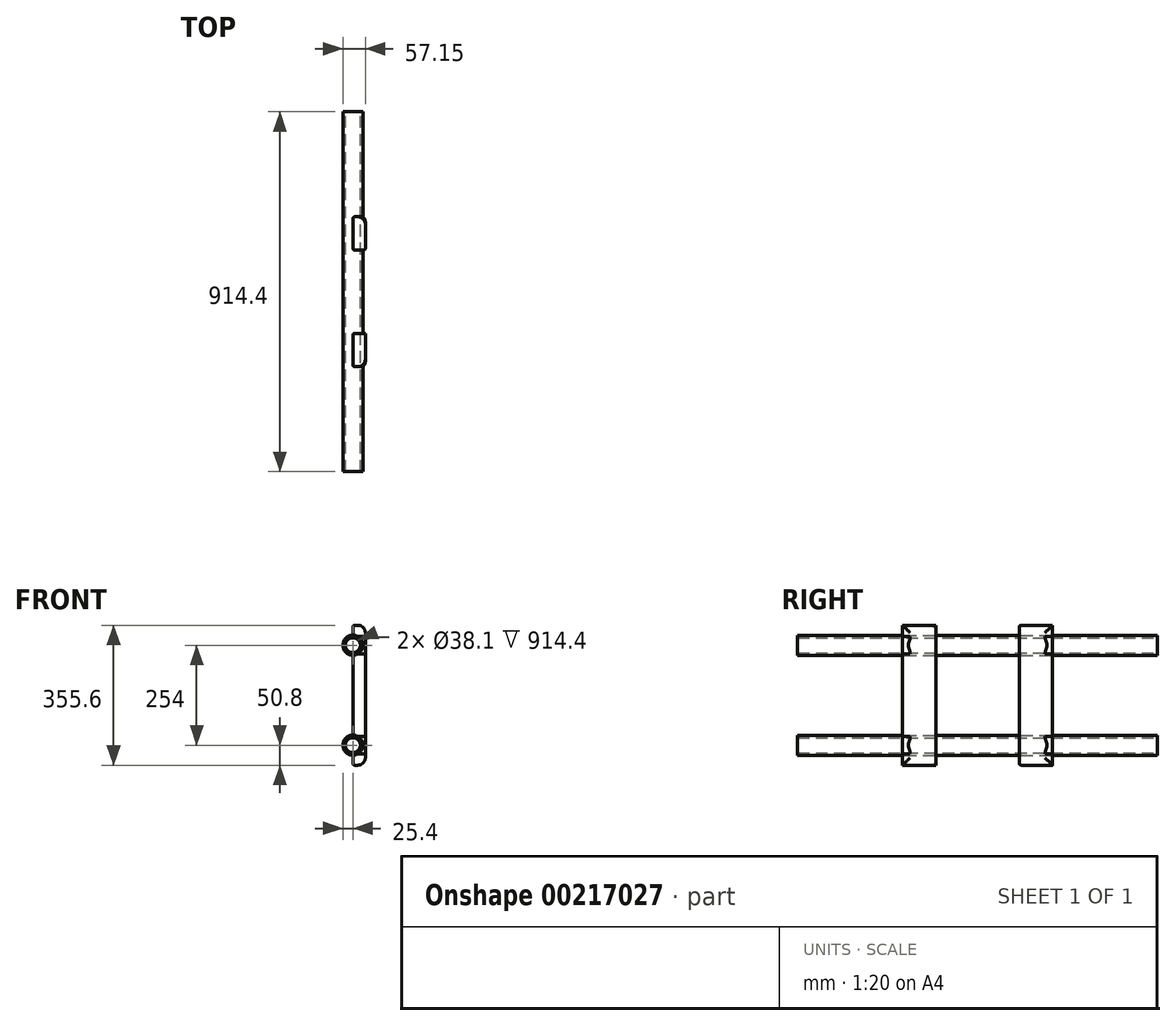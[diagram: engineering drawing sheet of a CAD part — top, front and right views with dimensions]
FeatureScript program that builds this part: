
annotation { "Feature Type Name" : "Feature", "Feature Type Description" : "" }
export const myFeature = defineFeature(function(context is Context, id is Id, definition is map)
    precondition{}
    {
        {
            var Q0;
            Q0=qCreatedBy(makeId("Front.planeOp"),FACE);
            var sketch = newSketch(context, id + "F0", { "sketchPlane" : qUnion([Q0])});
            skLineSegment(sketch, "E0", {"start": v(0, 0) * mm, "end": v(0, 76.2) * mm, "construction": true});
            skLineSegment(sketch, "E1", {"start": v(0, 76.2) * mm, "end": v(0, 0) * mm, "construction": true});
            skLineSegment(sketch, "E2", {"start": v(0, 0) * mm, "end": v(0, -76.2) * mm, "construction": true});
            skCircle(sketch, "E3", {"center": v(0, -76.2) * mm, "radius": 25.4 * mm});
            skCircle(sketch, "E4", {"center": v(0, -76.2) * mm, "radius": 19.05 * mm});
            skLineSegment(sketch, "E5", {"start": v(0, 101.6) * mm, "end": v(0, 127) * mm});
            skLineSegment(sketch, "E6", {"start": v(0, -101.6) * mm, "end": v(0, -127) * mm});
            skLineSegment(sketch, "E7", {"start": v(0, -127) * mm, "end": v(31.75, -127) * mm});
            skLineSegment(sketch, "E8", {"start": v(31.75, -127) * mm, "end": v(31.75, 127) * mm});
            skLineSegment(sketch, "E9", {"start": v(0, 50.8) * mm, "end": v(0, -50.8) * mm});
            skLineSegment(sketch, "E10", {"start": v(0, 0) * mm, "end": v(0, 177.8) * mm});
            skCircle(sketch, "E11", {"center": v(0, 177.8) * mm, "radius": 25.4 * mm});
            skCircle(sketch, "E12", {"center": v(0, 177.8) * mm, "radius": 19.05 * mm});
            skLineSegment(sketch, "E13", {"start": v(0, 203.2) * mm, "end": v(0, 228.6) * mm});
            skLineSegment(sketch, "E14", {"start": v(0, 228.6) * mm, "end": v(31.75, 228.6) * mm});
            skLineSegment(sketch, "E15", {"start": v(31.75, 228.6) * mm, "end": v(31.75, 127) * mm});
            skSolve(sketch);
        }
        {
            var Q0;
            {var subQ0=sQuery(id+"F0.wireOp",EDGE,"E6");Q0=makeQuery(id+"F0.imprint","IMPRINT",FACE,{"disambiguationData":[TD([[makeQuery(id+"F0.imprint","IMPRINT",EDGE,{"derivedFrom":subQ0}),1.0]])]});}
            extrude(context, id + "F1", {"entities" : qUnion([Q0]), "depth" : 381 * mm, "symmetric" : true});
        }
        {
            var Q0;
            Q0=makeQuery(id+"F1.opExtrude","SWEPT_FACE",FACE,{"disambiguationData":[OSD([sQuery(id+"F0.wireOp",EDGE,"E8"),sQuery(id+"F0.wireOp",EDGE,"E15")])]});
            var sketch = newSketch(context, id + "F2", { "sketchPlane" : qUnion([Q0])});
            skLineSegment(sketch, "E16.bottom", {"start": v(105.61, -155.17) * mm, "end": v(-105.61, -155.17) * mm});
            skLineSegment(sketch, "E16.top", {"start": v(105.61, 256.77) * mm, "end": v(-105.61, 256.77) * mm});
            skLineSegment(sketch, "E16.left", {"start": v(105.61, -155.17) * mm, "end": v(105.61, 256.77) * mm});
            skLineSegment(sketch, "E16.right", {"start": v(-105.61, -155.17) * mm, "end": v(-105.61, 256.77) * mm});
            skPoint(sketch, "E16.middle", {"position": v(0, 50.8) * mm});
            skPoint(sketch, "E16.middle.positionSnap0", {"position": v(-190.5, 50.8) * mm});
            skPoint(sketch, "E16.middle.positionSnap1", {"position": v(0, 228.6) * mm});
            skPoint(sketch, "E16.centerSnap0", {"position": v(-190.5, 50.8) * mm});
            skPoint(sketch, "E16.centerSnap1", {"position": v(0, 228.6) * mm});
            skSolve(sketch);
        }
        {
            var Q0;
            Q0 = qSketchRegion(id + "F2", true);
            extrude(context, id + "F3", {"entities" : qUnion([Q0]), "operationType" : NewBodyOperationType.REMOVE, "endBound" : BoundingType.THROUGH_ALL, "oppositeDirection" : true, "depth" : 25.4 * mm});
        }
        {
            var Q0;
            Q0=makeQuery(id+"F0.imprint","IMPRINT",FACE,{"disambiguationData":[TD([[makeQuery(id+"F0.imprint","IMPRINT",EDGE,{"derivedFrom":sQuery(id+"F0.wireOp",EDGE,"E12")}),-1.0]])]});
            extrude(context, id + "F4", {"entities" : qUnion([Q0]), "depth" : 25.4 * mm});
        }
        {
            var Q0;
            Q0=makeQuery(id+"F0.imprint","IMPRINT",FACE,{"disambiguationData":[TD([[makeQuery(id+"F0.imprint","IMPRINT",EDGE,{"derivedFrom":sQuery(id+"F0.wireOp",EDGE,"E4")}),-1.0]])]});
            var Q1;
            Q1=makeQuery(id+"F0.imprint","IMPRINT",FACE,{"disambiguationData":[TD([[makeQuery(id+"F0.imprint","IMPRINT",EDGE,{"derivedFrom":sQuery(id+"F0.wireOp",EDGE,"E12")}),-1.0]])]});
            extrude(context, id + "F5", {"entities" : qUnion([Q0, Q1]), "operationType" : NewBodyOperationType.ADD, "depth" : 914.4 * mm, "symmetric" : true});
        }
        {
            var Q0;
            Q0=makeQuery(id+"F1.opExtrude","CAP_EDGE",EDGE,{"disambiguationData":[OSD([sQuery(id+"F0.wireOp",EDGE,"E8"),sQuery(id+"F0.wireOp",EDGE,"E15")])],"isStart":false});
            var Q1;
            Q1=makeQuery(id+"F3.boolean.opBoolean","COPY",EDGE,{"derivedFrom":makeQuery(id+"F3.opExtrude","CAP_EDGE",EDGE,{"disambiguationData":[OSD([sQuery(id+"F2.wireOp",EDGE,"E16.right")])],"isStart":true})});
            var Q2;
            Q2=makeQuery(id+"F3.boolean.opBoolean","COPY",EDGE,{"derivedFrom":makeQuery(id+"F3.opExtrude","CAP_EDGE",EDGE,{"disambiguationData":[OSD([sQuery(id+"F2.wireOp",EDGE,"E16.left")])],"isStart":true})});
            var Q3;
            Q3=makeQuery(id+"F1.opExtrude","CAP_EDGE",EDGE,{"disambiguationData":[OSD([sQuery(id+"F0.wireOp",EDGE,"E8"),sQuery(id+"F0.wireOp",EDGE,"E15")])],"isStart":true});
            var Q4;
            {var subQ0=sQuery(id+"F0.wireOp",EDGE,"E15");var subQ1=sQuery(id+"F0.wireOp",EDGE,"E14");Q4=makeQuery(id+"F3.boolean.opBoolean","SPLIT",EDGE,{"disambiguationData":[TD([makeQuery(id+"F3.opExtrude","SWEPT_FACE",FACE,{"disambiguationData":[OSD([sQuery(id+"F2.wireOp",EDGE,"E16.right")])]})])],"derivedFrom":makeQuery(id+"F1.opExtrude","SWEPT_EDGE",EDGE,{"disambiguationData":[OSD([subQ1,subQ0])]})});}
            var Q5;
            {var subQ0=sQuery(id+"F0.wireOp",EDGE,"E15");var subQ1=sQuery(id+"F0.wireOp",EDGE,"E14");Q5=makeQuery(id+"F3.boolean.opBoolean","SPLIT",EDGE,{"disambiguationData":[TD([makeQuery(id+"F3.opExtrude","SWEPT_FACE",FACE,{"disambiguationData":[OSD([sQuery(id+"F2.wireOp",EDGE,"E16.left")])]})])],"derivedFrom":makeQuery(id+"F1.opExtrude","SWEPT_EDGE",EDGE,{"disambiguationData":[OSD([subQ1,subQ0])]})});}
            var Q6;
            {var subQ1=sQuery(id+"F0.wireOp",EDGE,"E8");var subQ2=sQuery(id+"F0.wireOp",EDGE,"E7");Q6=makeQuery(id+"F3.boolean.opBoolean","SPLIT",EDGE,{"disambiguationData":[TD([makeQuery(id+"F3.opExtrude","SWEPT_FACE",FACE,{"disambiguationData":[OSD([sQuery(id+"F2.wireOp",EDGE,"E16.left")])]})])],"derivedFrom":makeQuery(id+"F1.opExtrude","SWEPT_EDGE",EDGE,{"disambiguationData":[OSD([subQ2,subQ1])]})});}
            var Q7;
            {var subQ1=sQuery(id+"F0.wireOp",EDGE,"E8");var subQ2=sQuery(id+"F0.wireOp",EDGE,"E7");Q7=makeQuery(id+"F3.boolean.opBoolean","SPLIT",EDGE,{"disambiguationData":[TD([makeQuery(id+"F3.opExtrude","SWEPT_FACE",FACE,{"disambiguationData":[OSD([sQuery(id+"F2.wireOp",EDGE,"E16.right")])]})])],"derivedFrom":makeQuery(id+"F1.opExtrude","SWEPT_EDGE",EDGE,{"disambiguationData":[OSD([subQ2,subQ1])]})});}
            fillet(context, id + "F6", {"entities" : qUnion([Q0, Q1, Q2, Q3, Q4, Q5, Q6, Q7]), "radius" : 19.05 * mm, "tangentPropagation" : true, "allowEdgeOverflow" : false});
        }
        {
            var Q0;
            Q0=makeQuery(id+"F3.boolean.opBoolean","INTERSECT",EDGE,{"derivedFrom":[makeQuery(id+"F1.opExtrude","SWEPT_FACE",FACE,{"disambiguationData":[OSD([sQuery(id+"F0.wireOp",EDGE,"E9"),sQuery(id+"F0.wireOp",EDGE,"E10")])]}),makeQuery(id+"F3.opExtrude","SWEPT_FACE",FACE,{"disambiguationData":[OSD([sQuery(id+"F2.wireOp",EDGE,"E16.left")])]})]});
            var Q1;
            Q1=makeQuery(id+"F1.opExtrude","CAP_EDGE",EDGE,{"disambiguationData":[OSD([sQuery(id+"F0.wireOp",EDGE,"E9"),sQuery(id+"F0.wireOp",EDGE,"E10")])],"isStart":false});
            var Q2;
            Q2=makeQuery(id+"F1.opExtrude","CAP_EDGE",EDGE,{"disambiguationData":[OSD([sQuery(id+"F0.wireOp",EDGE,"E13")])],"isStart":false});
            var Q3;
            {var subQ0=sQuery(id+"F0.wireOp",EDGE,"E14");var subQ1=sQuery(id+"F0.wireOp",EDGE,"E13");Q3=makeQuery(id+"F3.boolean.opBoolean","SPLIT",EDGE,{"disambiguationData":[TD([makeQuery(id+"F3.opExtrude","SWEPT_FACE",FACE,{"disambiguationData":[OSD([sQuery(id+"F2.wireOp",EDGE,"E16.right")])]})])],"derivedFrom":makeQuery(id+"F1.opExtrude","SWEPT_EDGE",EDGE,{"disambiguationData":[OSD([subQ1,subQ0])]})});}
            var Q4;
            Q4=makeQuery(id+"F3.boolean.opBoolean","INTERSECT",EDGE,{"derivedFrom":[makeQuery(id+"F1.opExtrude","SWEPT_FACE",FACE,{"disambiguationData":[OSD([sQuery(id+"F0.wireOp",EDGE,"E13")])]}),makeQuery(id+"F3.opExtrude","SWEPT_FACE",FACE,{"disambiguationData":[OSD([sQuery(id+"F2.wireOp",EDGE,"E16.right")])]})]});
            var Q5;
            Q5=makeQuery(id+"F3.boolean.opBoolean","INTERSECT",EDGE,{"derivedFrom":[makeQuery(id+"F1.opExtrude","SWEPT_FACE",FACE,{"disambiguationData":[OSD([sQuery(id+"F0.wireOp",EDGE,"E9"),sQuery(id+"F0.wireOp",EDGE,"E10")])]}),makeQuery(id+"F3.opExtrude","SWEPT_FACE",FACE,{"disambiguationData":[OSD([sQuery(id+"F2.wireOp",EDGE,"E16.right")])]})]});
            var Q6;
            Q6=makeQuery(id+"F3.boolean.opBoolean","INTERSECT",EDGE,{"derivedFrom":[makeQuery(id+"F1.opExtrude","SWEPT_FACE",FACE,{"disambiguationData":[OSD([sQuery(id+"F0.wireOp",EDGE,"E6")])]}),makeQuery(id+"F3.opExtrude","SWEPT_FACE",FACE,{"disambiguationData":[OSD([sQuery(id+"F2.wireOp",EDGE,"E16.right")])]})]});
            var Q7;
            {var subQ0=sQuery(id+"F0.wireOp",EDGE,"E7");var subQ1=sQuery(id+"F0.wireOp",EDGE,"E6");Q7=makeQuery(id+"F3.boolean.opBoolean","SPLIT",EDGE,{"disambiguationData":[TD([makeQuery(id+"F3.opExtrude","SWEPT_FACE",FACE,{"disambiguationData":[OSD([sQuery(id+"F2.wireOp",EDGE,"E16.right")])]})])],"derivedFrom":makeQuery(id+"F1.opExtrude","SWEPT_EDGE",EDGE,{"disambiguationData":[OSD([subQ1,subQ0])]})});}
            var Q8;
            Q8=makeQuery(id+"F1.opExtrude","CAP_EDGE",EDGE,{"disambiguationData":[OSD([sQuery(id+"F0.wireOp",EDGE,"E6")])],"isStart":false});
            var Q9;
            Q9=makeQuery(id+"F3.boolean.opBoolean","INTERSECT",EDGE,{"derivedFrom":[makeQuery(id+"F1.opExtrude","SWEPT_FACE",FACE,{"disambiguationData":[OSD([sQuery(id+"F0.wireOp",EDGE,"E6")])]}),makeQuery(id+"F3.opExtrude","SWEPT_FACE",FACE,{"disambiguationData":[OSD([sQuery(id+"F2.wireOp",EDGE,"E16.left")])]})]});
            var Q10;
            Q10=makeQuery(id+"F1.opExtrude","CAP_EDGE",EDGE,{"disambiguationData":[OSD([sQuery(id+"F0.wireOp",EDGE,"E9"),sQuery(id+"F0.wireOp",EDGE,"E10")])],"isStart":true});
            var Q11;
            Q11=makeQuery(id+"F1.opExtrude","CAP_EDGE",EDGE,{"disambiguationData":[OSD([sQuery(id+"F0.wireOp",EDGE,"E6")])],"isStart":true});
            var Q12;
            {var subQ0=sQuery(id+"F0.wireOp",EDGE,"E7");var subQ1=sQuery(id+"F0.wireOp",EDGE,"E6");Q12=makeQuery(id+"F3.boolean.opBoolean","SPLIT",EDGE,{"disambiguationData":[TD([makeQuery(id+"F3.opExtrude","SWEPT_FACE",FACE,{"disambiguationData":[OSD([sQuery(id+"F2.wireOp",EDGE,"E16.left")])]})])],"derivedFrom":makeQuery(id+"F1.opExtrude","SWEPT_EDGE",EDGE,{"disambiguationData":[OSD([subQ1,subQ0])]})});}
            var Q13;
            Q13=makeQuery(id+"F3.boolean.opBoolean","INTERSECT",EDGE,{"derivedFrom":[makeQuery(id+"F1.opExtrude","SWEPT_FACE",FACE,{"disambiguationData":[OSD([sQuery(id+"F0.wireOp",EDGE,"E13")])]}),makeQuery(id+"F3.opExtrude","SWEPT_FACE",FACE,{"disambiguationData":[OSD([sQuery(id+"F2.wireOp",EDGE,"E16.left")])]})]});
            var Q14;
            {var subQ0=sQuery(id+"F0.wireOp",EDGE,"E14");var subQ1=sQuery(id+"F0.wireOp",EDGE,"E13");Q14=makeQuery(id+"F3.boolean.opBoolean","SPLIT",EDGE,{"disambiguationData":[TD([makeQuery(id+"F3.opExtrude","SWEPT_FACE",FACE,{"disambiguationData":[OSD([sQuery(id+"F2.wireOp",EDGE,"E16.left")])]})])],"derivedFrom":makeQuery(id+"F1.opExtrude","SWEPT_EDGE",EDGE,{"disambiguationData":[OSD([subQ1,subQ0])]})});}
            var Q15;
            Q15=makeQuery(id+"F3.boolean.opBoolean","INTERSECT",EDGE,{"derivedFrom":[makeQuery(id+"F1.opExtrude","SWEPT_FACE",FACE,{"disambiguationData":[OSD([sQuery(id+"F0.wireOp",EDGE,"E14")])]}),makeQuery(id+"F3.opExtrude","SWEPT_FACE",FACE,{"disambiguationData":[OSD([sQuery(id+"F2.wireOp",EDGE,"E16.left")])]})]});
            var Q16;
            Q16=makeQuery(id+"F1.opExtrude","CAP_EDGE",EDGE,{"disambiguationData":[OSD([sQuery(id+"F0.wireOp",EDGE,"E13")])],"isStart":true});
            fillet(context, id + "F7", {"entities" : qUnion([Q0, Q1, Q2, Q3, Q4, Q5, Q6, Q7, Q8, Q9, Q10, Q11, Q12, Q13, Q14, Q15, Q16]), "radius" : 5.08 * mm, "tangentPropagation" : true, "allowEdgeOverflow" : false});
        }
    });
